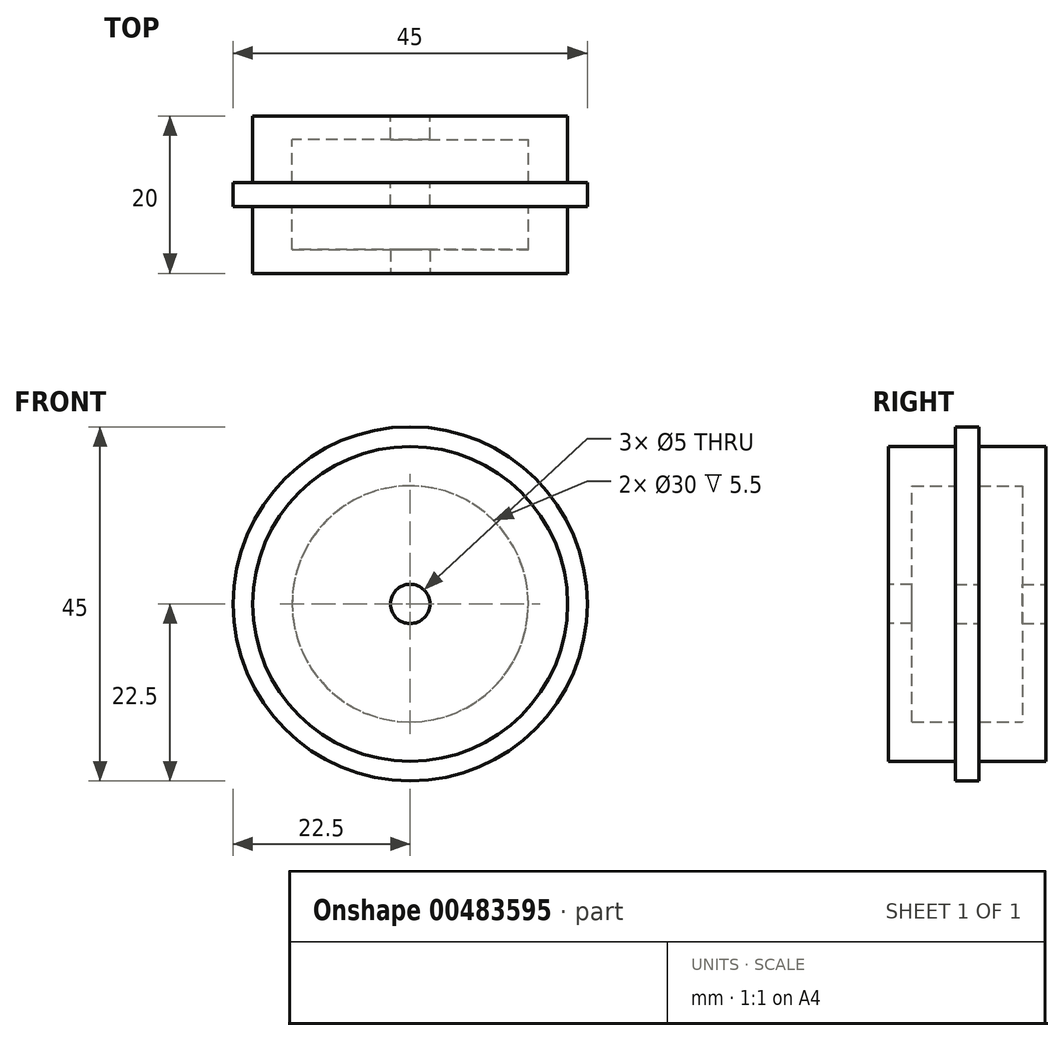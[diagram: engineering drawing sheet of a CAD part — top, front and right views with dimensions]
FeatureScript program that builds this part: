
annotation { "Feature Type Name" : "Feature", "Feature Type Description" : "" }
export const myFeature = defineFeature(function(context is Context, id is Id, definition is map)
    precondition{}
    {
        {
            var Q0;
            Q0=qCreatedBy(makeId("Front.planeOp"),FACE);
            var sketch = newSketch(context, id + "F0", { "sketchPlane" : qUnion([Q0])});
            skCircle(sketch, "E0", {"center": v(0, 0) * mm, "radius": 20 * mm});
            skCircle(sketch, "E1.0", {"center": v(0, 0) * mm, "radius": 15 * mm});
            skSolve(sketch);
        }
        {
            var Q0;
            Q0 = qSketchRegion(id + "F0", true);
            extrude(context, id + "F1", {"entities" : qUnion([Q0]), "depth" : 10 * mm});
        }
        {
            var Q0;
            Q0=makeQuery(id+"F1.opExtrude","SWEPT_BODY",BODY,{"disambiguationData":[OSD([sQuery(id+"F0.wireOp",EDGE,"E0"),sQuery(id+"F0.wireOp",EDGE,"E1.0")])]});
            var Q1;
            Q1=qCreatedBy(makeId("Front.planeOp"),FACE);
            mirror(context, id + "F2", {"operationType" : NewBodyOperationType.ADD, "entities" : qUnion([Q0]), "mirrorPlane" : qUnion([Q1])});
        }
        {
            var Q0;
            Q0=qCreatedBy(makeId("Front.planeOp"),FACE);
            var sketch = newSketch(context, id + "F3", { "sketchPlane" : qUnion([Q0])});
            skCircle(sketch, "E2", {"center": v(0, 0) * mm, "radius": 22.5 * mm});
            skCircle(sketch, "E3.0", {"center": v(0, 0) * mm, "radius": 2.5 * mm});
            skSolve(sketch);
        }
        {
            var Q0;
            Q0 = qSketchRegion(id + "F3", true);
            extrude(context, id + "F4", {"entities" : qUnion([Q0]), "operationType" : NewBodyOperationType.ADD, "depth" : 1.5 * mm});
        }
        {
            var Q0;
            Q0=makeQuery(id+"F1.opExtrude","SWEPT_BODY",BODY,{"disambiguationData":[OSD([sQuery(id+"F0.wireOp",EDGE,"E0"),sQuery(id+"F0.wireOp",EDGE,"E1.0")])]});
            var Q1;
            Q1=qCreatedBy(makeId("Front.planeOp"),FACE);
            mirror(context, id + "F5", {"operationType" : NewBodyOperationType.ADD, "entities" : qUnion([Q0]), "mirrorPlane" : qUnion([Q1])});
        }
        {
            var Q0;
            Q0=makeQuery(id+"F1.opExtrude","CAP_FACE",FACE,{"disambiguationData":[OSD([sQuery(id+"F0.wireOp",EDGE,"E0"),sQuery(id+"F0.wireOp",EDGE,"E1.0")])],"isStart":false});
            cPlane(context, id + "F6", {"entities" : qUnion([Q0]), "cplaneType" : CPlaneType.OFFSET, "offset" : 0 * mm, "width" : 150 * mm, "height" : 150 * mm});
        }
        {
            var Q0;
            Q0=qCreatedBy(id+"F6.planeOp",FACE);
            var sketch = newSketch(context, id + "F7", { "sketchPlane" : qUnion([Q0])});
            skCircle(sketch, "E4", {"center": v(0, 0) * mm, "radius": 15 * mm});
            skCircle(sketch, "E5.0", {"center": v(0, 0) * mm, "radius": 2.5 * mm});
            skSolve(sketch);
        }
        {
            var Q0;
            Q0=makeQuery(id+"F7.imprint","IMPRINT",FACE,{"disambiguationData":[TD([[makeQuery(id+"F7.imprint","IMPRINT",EDGE,{"derivedFrom":sQuery(id+"F7.wireOp",EDGE,"E4")}),1.0]])]});
            var Q1;
            Q1 = qConstructionFilter(qBodyType(qCreatedBy(id + "F7" ,EDGE), BodyType.WIRE), ConstructionObject.NO);
            extrude(context, id + "F8", {"entities" : qUnion([Q0]), "surfaceEntities" : qUnion([Q1]), "oppositeDirection" : true, "depth" : 3 * mm});
        }
        {
            var Q0;
            Q0=makeQuery(id+"F8.opExtrude","SWEPT_BODY",BODY,{"disambiguationData":[OSD([sQuery(id+"F7.wireOp",EDGE,"E4"),sQuery(id+"F7.wireOp",EDGE,"E5.0")])]});
            var Q1;
            Q1=qCreatedBy(makeId("Front.planeOp"),FACE);
            mirror(context, id + "F9", {"operationType" : NewBodyOperationType.ADD, "entities" : qUnion([Q0]), "mirrorPlane" : qUnion([Q1])});
        }
    });
